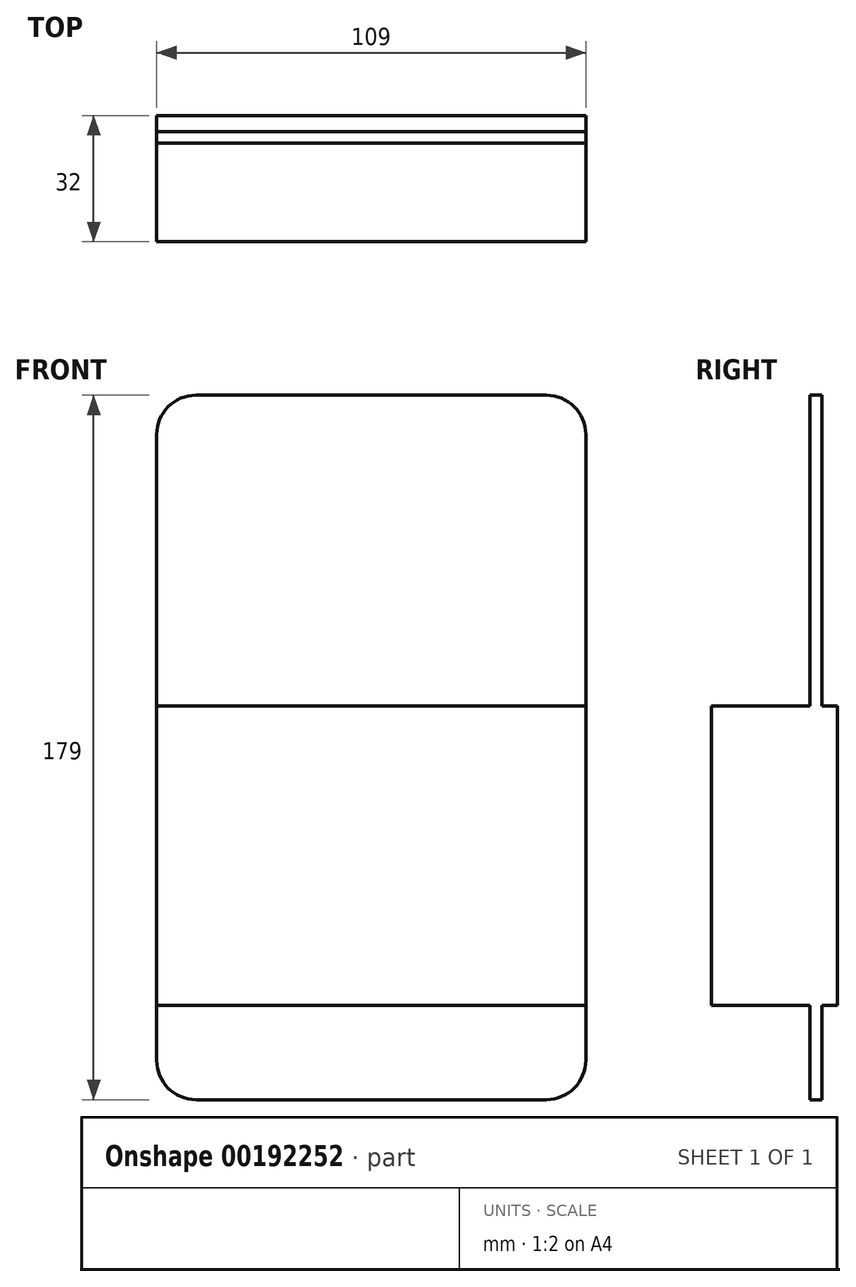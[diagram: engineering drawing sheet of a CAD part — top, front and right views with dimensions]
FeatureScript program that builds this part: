
annotation { "Feature Type Name" : "Feature", "Feature Type Description" : "" }
export const myFeature = defineFeature(function(context is Context, id is Id, definition is map)
    precondition{}
    {
        {
            var Q0;
            Q0=qCreatedBy(makeId("Front.planeOp"),FACE);
            var sketch = newSketch(context, id + "F0", { "sketchPlane" : qUnion([Q0])});
            skLineSegment(sketch, "E0.bottom", {"start": v(54.5, -89.5) * mm, "end": v(-54.5, -89.5) * mm});
            skLineSegment(sketch, "E0.top", {"start": v(54.5, 89.5) * mm, "end": v(-54.5, 89.5) * mm});
            skLineSegment(sketch, "E0.left", {"start": v(54.5, -89.5) * mm, "end": v(54.5, 89.5) * mm});
            skLineSegment(sketch, "E0.right", {"start": v(-54.5, -89.5) * mm, "end": v(-54.5, 89.5) * mm});
            skPoint(sketch, "E0.middle", {"position": v(0, 0) * mm});
            skSolve(sketch);
        }
        {
            var Q0;
            Q0=makeQuery(id+"F0.imprint","IMPRINT",FACE,{"disambiguationData":[TD([[makeQuery(id+"F0.imprint","IMPRINT",EDGE,{"derivedFrom":sQuery(id+"F0.wireOp",EDGE,"E0.bottom")}),-1.0]])]});
            extrude(context, id + "F1", {"entities" : qUnion([Q0]), "depth" : 3 * mm});
        }
        {
            var Q0;
            Q0=makeQuery(id+"F1.opExtrude","SWEPT_EDGE",EDGE,{"disambiguationData":[OSD([sQuery(id+"F0.wireOp",EDGE,"E0.top"),sQuery(id+"F0.wireOp",EDGE,"E0.left")])]});
            var Q1;
            Q1=makeQuery(id+"F1.opExtrude","SWEPT_EDGE",EDGE,{"disambiguationData":[OSD([sQuery(id+"F0.wireOp",EDGE,"E0.top"),sQuery(id+"F0.wireOp",EDGE,"E0.right")])]});
            var Q2;
            Q2=makeQuery(id+"F1.opExtrude","SWEPT_EDGE",EDGE,{"disambiguationData":[OSD([sQuery(id+"F0.wireOp",EDGE,"E0.bottom"),sQuery(id+"F0.wireOp",EDGE,"E0.left")])]});
            var Q3;
            Q3=makeQuery(id+"F1.opExtrude","SWEPT_EDGE",EDGE,{"disambiguationData":[OSD([sQuery(id+"F0.wireOp",EDGE,"E0.bottom"),sQuery(id+"F0.wireOp",EDGE,"E0.right")])]});
            fillet(context, id + "F2", {"entities" : qUnion([Q0, Q1, Q2, Q3]), "radius" : 10 * mm, "tangentPropagation" : true, "allowEdgeOverflow" : false});
        }
        {
            var Q0;
            Q0=makeQuery(id+"F1.opExtrude","CAP_FACE",FACE,{"disambiguationData":[OSD([sQuery(id+"F0.wireOp",EDGE,"E0.bottom"),sQuery(id+"F0.wireOp",EDGE,"E0.top"),sQuery(id+"F0.wireOp",EDGE,"E0.left"),sQuery(id+"F0.wireOp",EDGE,"E0.right")])],"isStart":false});
            var sketch = newSketch(context, id + "F3", { "sketchPlane" : qUnion([Q0])});
            skLineSegment(sketch, "E1.bottom", {"start": v(-54.5, 10.5) * mm, "end": v(54.5, 10.5) * mm});
            skLineSegment(sketch, "E1.top", {"start": v(-54.5, -65.5) * mm, "end": v(54.5, -65.5) * mm});
            skLineSegment(sketch, "E1.left", {"start": v(-54.5, 10.5) * mm, "end": v(-54.5, -65.5) * mm});
            skLineSegment(sketch, "E1.right", {"start": v(54.5, 10.5) * mm, "end": v(54.5, -65.5) * mm});
            skSolve(sketch);
        }
        {
            var Q0;
            Q0 = qSketchRegion(id + "F3", true);
            extrude(context, id + "F4", {"entities" : qUnion([Q0]), "operationType" : NewBodyOperationType.ADD, "depth" : 25 * mm, "hasSecondDirection" : true, "secondDirectionOppositeDirection" : true, "secondDirectionDepth" : 7 * mm});
        }
    });
